# Revit family: PT, PS, 126, 129, 156, 1212, 159, 1515, 189, 1512,1812,186, 216, 246
name_source: partatom
category: Windows
revit_build: Autodesk Revit LT 2016 (Build: 20150220_1215(x64)
units: mm (PartAtom-declared; Revit-internal decimal feet)

## family parameters
Always vertical = Yes
Cut with Voids When Loaded = No
Host = Wall
OmniClass Number = 23.30.20.00
OmniClass Title = Windows
Room Calculation Point = No
Shared = No

## types (11) — shared parameters
Aluminium anodized = Aluminium
Default Sill Height = 914 mm
Glazing = Glass
Manufacturer = Robmeg
Plaster = 5 mm  [stored 0.0164042 ft]
Rough Height = 1219 mm
URL = http://www.robmeg.co.za
Wall Closure = By host

## per-type parameters (varying)
| type | Centre vert mullion | Description | Height | Model | Side hung | Top hung | Width |
| PT Type- 126 | 595 mm | Anodized Aluminium | 610 mm  [stored 2.00131 ft] | PT 126 | No | Yes | 1200 mm |
| PT Type- 156 | 595 mm | Anodized Alumium | 610 mm  [stored 2.00131 ft] | PT 156 | No | Yes | 1500 mm  [stored 4.92126 ft] |
| PT Type- 186 | 900 mm  [stored 2.95276 ft] | Anodized Aluminium | 610 mm  [stored 2.00131 ft] | PT 186 | No | Yes | 1800 mm  [stored 5.90551 ft] |
| PT Type- 216 | 800 mm  [stored 2.62467 ft] | Anodized Aluminium | 610 mm  [stored 2.00131 ft] | PT 216 | No | Yes | 2100 mm |
| PT Type- 246 | 800 mm  [stored 2.62467 ft] | Anodized Aluminium | 610 mm  [stored 2.00131 ft] | PT 246 | No | Yes | 2400 mm |
| PS Type- 129 | 610 mm  [stored 2.00131 ft] | Anodized Aluminium | 910 mm | PS 129 | Yes | No | 1210 mm  [stored 3.96982 ft] |
| PS Type- 1212 | 610 mm  [stored 2.00131 ft] | Anodized Aluminium | 1210 mm  [stored 3.96982 ft] | PS 1212 | Yes | No | 1210 mm  [stored 3.96982 ft] |
| PS Type- 189 | 610 mm  [stored 2.00131 ft] | Anodized Aluminium | 910 mm | PS 189 | Yes | No | 1810 mm  [stored 5.93832 ft] |
| PS Type- 1512 | 610 mm  [stored 2.00131 ft] | Anodized Aluminium | 910 mm | PS 152 | Yes | No | 1510 mm  [stored 4.95407 ft] |
| PS Type- 1812 | 610 mm  [stored 2.00131 ft] | Anodized Aluminium | 1210 mm  [stored 3.96982 ft] | PS 1812 | Yes | No | 1810 mm  [stored 5.93832 ft] |
| PS Type- 159 | 610 mm  [stored 2.00131 ft] | Anodized Aluminium | 910 mm | PS 159 | Yes | No | 1510 mm  [stored 4.95407 ft] |

note: [stored X ft] marks values corroborated as IEEE doubles in the binary element streams (Revit-internal decimal feet)

## geometry (parser evidence)
native form markers: Sweep x4
no freeform markers — native parametric forms only
